# Revit family: Faucet-Lavatory-KOHLER-TAUT-K-74026M
name_source: partatom
category: Plumbing Fixtures
units: mm (PartAtom-declared; Revit-internal decimal feet)

## family parameters
Cut with Voids When Loaded = No
Host = Face
Maintain Annotation Orientation = No
OmniClass Number = 23.31.11.00
OmniClass Title = Faucets
Part Type = Normal
Room Calculation Point = No
Round Connector Dimension = Use Diameter
Shared = No

## types (4) — shared parameters
ADA Compliant = No
Assembly Code = D2010
CW Connection = Yes
Cold Water Inlet = Cold Water Inlet
Date Modified = 04/07/2025
Default Elevation = 36"
Drain Included = Yes
Flow Rate = 2 GPM
HW Connection = Yes
Handle Clearance = 3 3/16"
Height = 10 11/16"
Hot Water Inlet = Hot Water Inlet
Length = 4 3/4"
Manufacturer = Kohler Co.
Master Format 2014 = 22 41 39
Master Format 2014 Name = Residential Faucets, Supplies, and Trim
Material = Premium Metal Construction
Product Name = Taut
Spout Reach = 4 3/4"
URL = https://la.kohler.com
Vent Connection = No
Waste Connection = No
Waste Water Outlet = Waste Water Outlet
WaterSense Certified = No
Width = 1 7/8"

## per-type parameters (varying)
| type | Description | Finish | Model | Pressure | Product Documentation Link | Product Page URL | Secondary Finish | Type |
| 2.2 GPM, CP-Polished Chrome | Single-lever high faucet for sink, 1.2 gal per min | Kohler-Metal-CP-Polished_Chrome | K-74026M-4-CP | 90.00 psi | https://techcomm.kohler.com | https://la.kohler.com | Plastic-Pantone-Cool_Gray_6C | 3 |
| 2.2 GPM, 0-White | Single-lever high faucet for sink, 1.2 gal per min | Kohler-Metal-0-White | K-74026M-4-0 | 90.00 psi |  |  | Plastic-Pantone-Cool_Gray_6C | 1 |
| 2.2 GPM, BL-Matte Black | Single-lever high faucet for sink, 1.2 gal per min | Kohler-Metal-BL-Matte_Black | K-74026M-4-BL | 90.00 psi | https://techcomm.kohler.com | https://la.kohler.com | Kohler-Plastic-7-Black_Black | 2 |
| 1.5 GPM, CP-Polished Chrome | Single-lever high faucet for washbasin, 1.5 gal per min | Kohler-Metal-CP-Polished_Chrome | K-74026M-4AB-CP | 60.00 psi |  | https://la.kohler.com | Plastic-Pantone-Cool_Gray_6C | 4 |

## geometry (parser evidence)
native form markers: Sweep x6
no freeform markers — native parametric forms only
